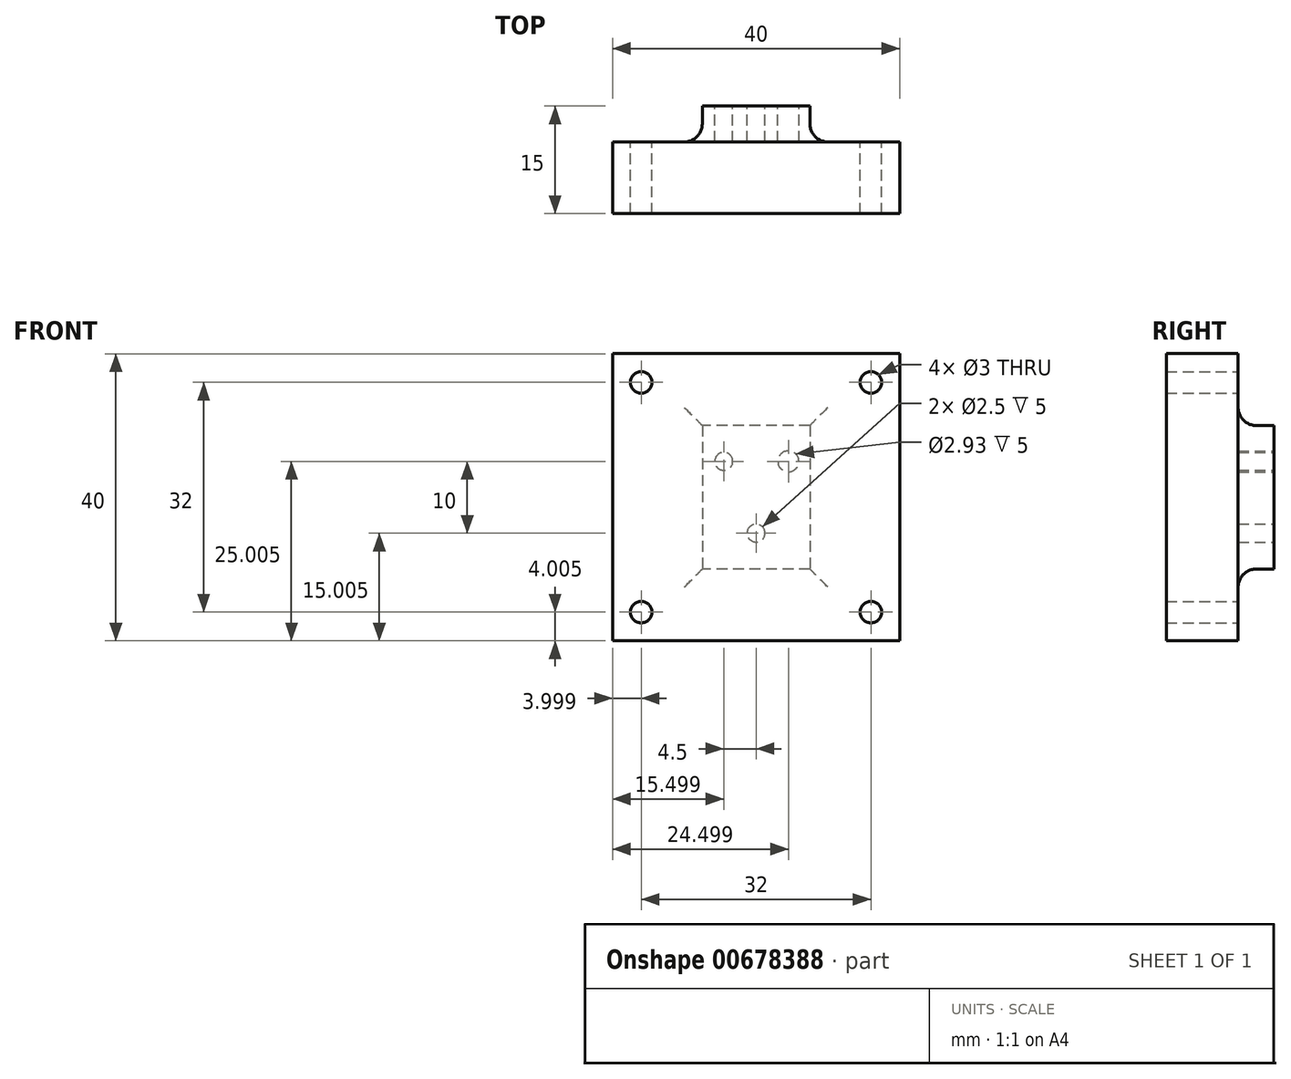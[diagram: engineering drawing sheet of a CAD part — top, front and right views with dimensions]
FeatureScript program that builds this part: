
annotation { "Feature Type Name" : "Feature", "Feature Type Description" : "" }
export const myFeature = defineFeature(function(context is Context, id is Id, definition is map)
    precondition{}
    {
        {
            var Q0;
            Q0=qCreatedBy(makeId("Front.planeOp"),FACE);
            var sketch = newSketch(context, id + "F0", { "sketchPlane" : qUnion([Q0])});
            skCircle(sketch, "E0", {"center": v(-2.25, 40.21) * mm, "radius": 1.25 * mm});
            skCircle(sketch, "E1", {"center": v(6.75, 40.21) * mm, "radius": 1.47 * mm});
            skCircle(sketch, "E2", {"center": v(2.25, 30.21) * mm, "radius": 1.25 * mm});
            skLineSegment(sketch, "E3", {"start": v(-12.65, 50.21) * mm, "end": v(-12.65, 20.21) * mm});
            skLineSegment(sketch, "E4", {"start": v(-2.25, 40.21) * mm, "end": v(2.25, 30.21) * mm, "construction": true});
            skLineSegment(sketch, "E5", {"start": v(6.75, 40.21) * mm, "end": v(2.25, 30.21) * mm, "construction": true});
            skLineSegment(sketch, "E6", {"start": v(-2.25, 40.21) * mm, "end": v(6.75, 40.21) * mm, "construction": true});
            skLineSegment(sketch, "E7", {"start": v(2.25, 30.21) * mm, "end": v(2.25, 40.21) * mm});
            skLineSegment(sketch, "E8.bottom", {"start": v(9.75, 45.21) * mm, "end": v(-5.25, 45.21) * mm});
            skLineSegment(sketch, "E8.top", {"start": v(9.75, 25.21) * mm, "end": v(-5.25, 25.21) * mm});
            skLineSegment(sketch, "E8.left", {"start": v(9.75, 45.21) * mm, "end": v(9.75, 25.21) * mm});
            skLineSegment(sketch, "E8.right", {"start": v(-5.25, 45.21) * mm, "end": v(-5.25, 25.21) * mm});
            skPoint(sketch, "E8.middle", {"position": v(2.25, 35.21) * mm});
            skSolve(sketch);
        }
        {
            var Q0;
            Q0=makeQuery(id+"F0.imprint","IMPRINT",FACE,{"disambiguationData":[TD([[makeQuery(id+"F0.imprint","IMPRINT",EDGE,{"derivedFrom":sQuery(id+"F0.wireOp",EDGE,"E0")}),-1.0]])]});
            extrude(context, id + "F1", {"entities" : qUnion([Q0]), "depth" : 5 * mm, "offsetDistance" : 25 * mm});
        }
        {
            var Q0;
            Q0=makeQuery(id+"F1.opExtrude","CAP_FACE",FACE,{"disambiguationData":[OSD([sQuery(id+"F0.wireOp",EDGE,"E0"),sQuery(id+"F0.wireOp",EDGE,"E1"),sQuery(id+"F0.wireOp",EDGE,"E2"),sQuery(id+"F0.wireOp",EDGE,"E8.bottom"),sQuery(id+"F0.wireOp",EDGE,"E8.top"),sQuery(id+"F0.wireOp",EDGE,"E8.left"),sQuery(id+"F0.wireOp",EDGE,"E8.right")])],"isStart":false});
            var sketch = newSketch(context, id + "F2", { "sketchPlane" : qUnion([Q0])});
            skLineSegment(sketch, "E9", {"start": v(9.75, 45.21) * mm, "end": v(-5.25, 25.21) * mm});
            skLineSegment(sketch, "E10.bottom", {"start": v(22.25, 55.21) * mm, "end": v(-17.75, 55.21) * mm});
            skLineSegment(sketch, "E10.top", {"start": v(22.25, 15.21) * mm, "end": v(-17.75, 15.21) * mm});
            skLineSegment(sketch, "E10.left", {"start": v(22.25, 55.21) * mm, "end": v(22.25, 15.21) * mm});
            skLineSegment(sketch, "E10.right", {"start": v(-17.75, 55.21) * mm, "end": v(-17.75, 15.21) * mm});
            skPoint(sketch, "E10.middle", {"position": v(2.25, 35.21) * mm});
            skLineSegment(sketch, "E11.bottom", {"start": v(18.25, 51.21) * mm, "end": v(-13.75, 51.21) * mm, "construction": true});
            skLineSegment(sketch, "E11.top", {"start": v(18.25, 19.21) * mm, "end": v(-13.75, 19.21) * mm, "construction": true});
            skLineSegment(sketch, "E11.left", {"start": v(18.25, 51.21) * mm, "end": v(18.25, 19.21) * mm, "construction": true});
            skLineSegment(sketch, "E11.right", {"start": v(-13.75, 51.21) * mm, "end": v(-13.75, 19.21) * mm, "construction": true});
            skCircle(sketch, "E12", {"center": v(-13.75, 51.21) * mm, "radius": 1.5 * mm});
            skCircle(sketch, "E13", {"center": v(18.25, 51.21) * mm, "radius": 1.5 * mm});
            skCircle(sketch, "E14", {"center": v(18.25, 19.21) * mm, "radius": 1.5 * mm});
            skCircle(sketch, "E15", {"center": v(-13.75, 19.21) * mm, "radius": 1.5 * mm});
            skSolve(sketch);
        }
        {
            var Q0;
            Q0=makeQuery(id+"F2.imprint","IMPRINT",FACE,{"disambiguationData":[TD([[makeQuery(id+"F2.imprint","IMPRINT",EDGE,{"derivedFrom":sQuery(id+"F2.wireOp",EDGE,"E10.bottom")}),1.0]])]});
            var Q1;
            Q1=makeQuery(id+"F2.imprint","IMPRINT",FACE,{"disambiguationData":[TD([[makeQuery(id+"F2.imprint","IMPRINT",EDGE,{"derivedFrom":makeQuery(id+"F1.opExtrude","CAP_EDGE",EDGE,{"disambiguationData":[OSD([sQuery(id+"F0.wireOp",EDGE,"E2")])],"isStart":false})}),-1.0]])]});
            var Q2;
            Q2=makeQuery(id+"F2.imprint","IMPRINT",FACE,{"disambiguationData":[TD([[makeQuery(id+"F2.imprint","IMPRINT",EDGE,{"derivedFrom":makeQuery(id+"F1.opExtrude","CAP_EDGE",EDGE,{"disambiguationData":[OSD([sQuery(id+"F0.wireOp",EDGE,"E0")])],"isStart":false})}),-1.0]])]});
            var Q3;
            {var subQ0=sQuery(id+"F2.wireOp",EDGE,"E9");var subQ1=makeQuery(id+"F1.opExtrude","CAP_EDGE",EDGE,{"disambiguationData":[OSD([sQuery(id+"F0.wireOp",EDGE,"E1")])],"isStart":false});var subQ2=makeQuery(id+"F2.imprint","INTERSECT",VERTEX,{"disambiguationData":[OD(0.0)],"derivedFrom":[subQ1,subQ0]});Q3=makeQuery(id+"F2.imprint","IMPRINT",FACE,{"disambiguationData":[TD([[makeQuery(id+"F2.imprint","IMPRINT",EDGE,{"disambiguationData":[TD([[subQ2,-1.0]])],"derivedFrom":subQ0}),1.0]])]});}
            var Q4;
            Q4=makeQuery(id+"F2.imprint","IMPRINT",FACE,{"disambiguationData":[TD([[makeQuery(id+"F2.imprint","IMPRINT",EDGE,{"derivedFrom":makeQuery(id+"F1.opExtrude","CAP_EDGE",EDGE,{"disambiguationData":[OSD([sQuery(id+"F0.wireOp",EDGE,"E0")])],"isStart":false})}),1.0]])]});
            var Q5;
            {var subQ0=sQuery(id+"F2.wireOp",EDGE,"E9");var subQ1=makeQuery(id+"F1.opExtrude","CAP_EDGE",EDGE,{"disambiguationData":[OSD([sQuery(id+"F0.wireOp",EDGE,"E1")])],"isStart":false});var subQ2=makeQuery(id+"F2.imprint","INTERSECT",VERTEX,{"disambiguationData":[OD(0.0)],"derivedFrom":[subQ1,subQ0]});Q5=makeQuery(id+"F2.imprint","IMPRINT",FACE,{"disambiguationData":[TD([[makeQuery(id+"F2.imprint","IMPRINT",EDGE,{"disambiguationData":[TD([[subQ2,-1.0]])],"derivedFrom":subQ0}),-1.0]])]});}
            var Q6;
            Q6=makeQuery(id+"F2.imprint","IMPRINT",FACE,{"disambiguationData":[TD([[makeQuery(id+"F2.imprint","IMPRINT",EDGE,{"derivedFrom":makeQuery(id+"F1.opExtrude","CAP_EDGE",EDGE,{"disambiguationData":[OSD([sQuery(id+"F0.wireOp",EDGE,"E2")])],"isStart":false})}),1.0]])]});
            extrude(context, id + "F3", {"entities" : qUnion([Q0, Q1, Q2, Q3, Q4, Q5, Q6]), "operationType" : NewBodyOperationType.ADD, "depth" : 10 * mm, "offsetDistance" : 25 * mm});
        }
        {
            var Q0;
            Q0=makeQuery(id+"F1.opExtrude","CAP_EDGE",EDGE,{"disambiguationData":[OSD([sQuery(id+"F0.wireOp",EDGE,"E8.right")])],"isStart":false});
            var Q1;
            Q1=makeQuery(id+"F1.opExtrude","CAP_EDGE",EDGE,{"disambiguationData":[OSD([sQuery(id+"F0.wireOp",EDGE,"E8.top")])],"isStart":false});
            var Q2;
            Q2=makeQuery(id+"F1.opExtrude","CAP_EDGE",EDGE,{"disambiguationData":[OSD([sQuery(id+"F0.wireOp",EDGE,"E8.left")])],"isStart":false});
            var Q3;
            Q3=makeQuery(id+"F1.opExtrude","CAP_EDGE",EDGE,{"disambiguationData":[OSD([sQuery(id+"F0.wireOp",EDGE,"E8.bottom")])],"isStart":false});
            fillet(context, id + "F4", {"entities" : qUnion([Q0, Q1, Q2, Q3]), "radius" : 2.5 * mm, "tangentPropagation" : true, "allowEdgeOverflow" : false});
        }
    });
